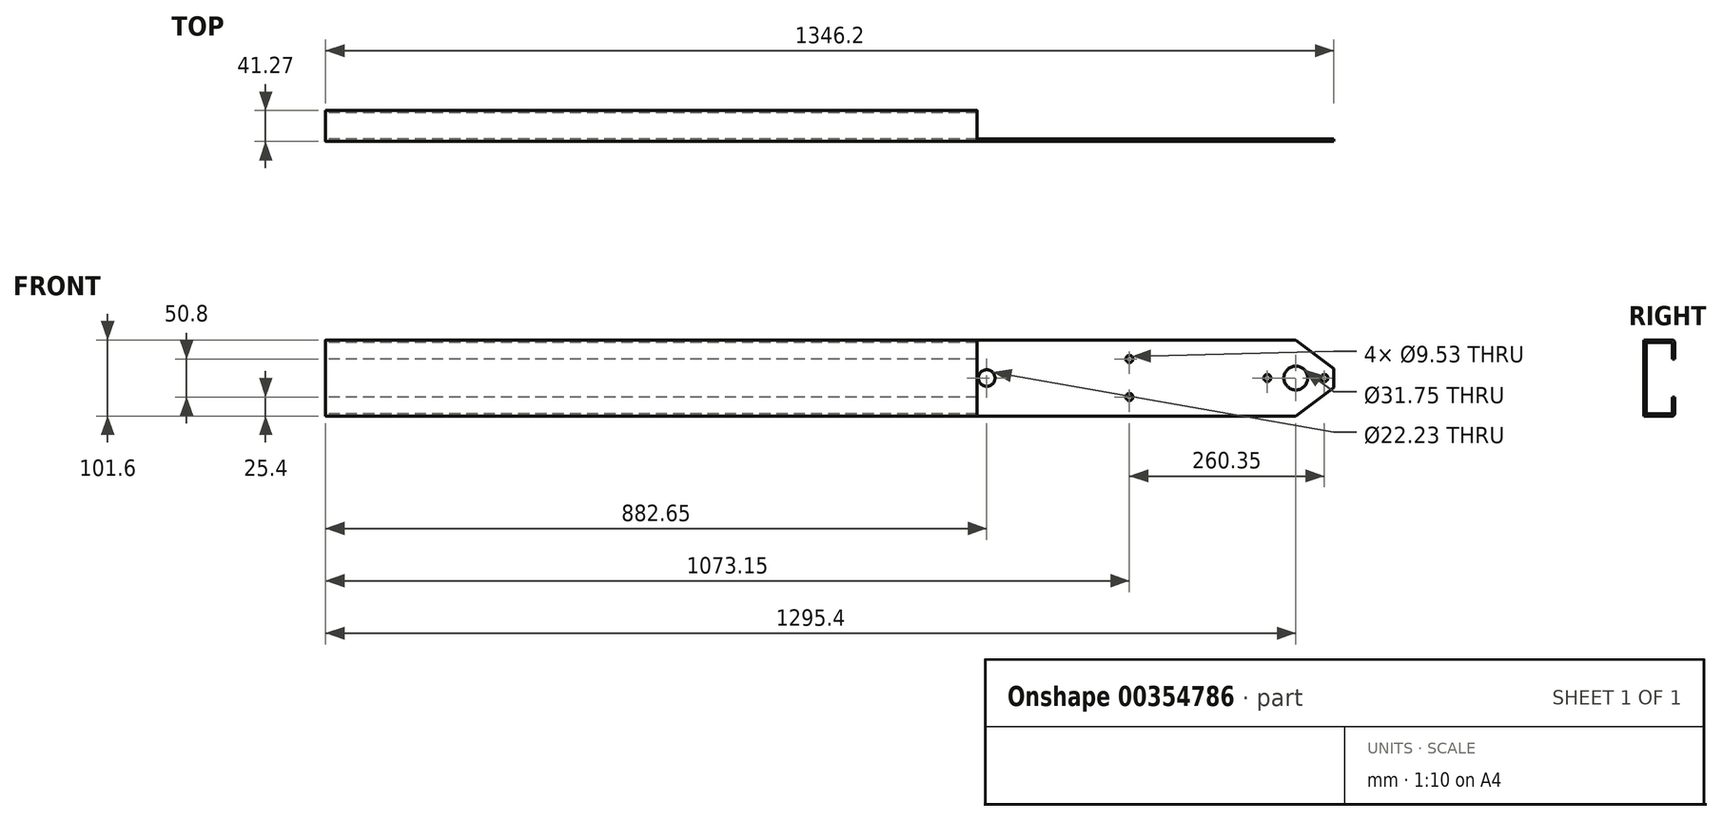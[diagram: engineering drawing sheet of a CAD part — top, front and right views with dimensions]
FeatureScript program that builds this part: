
annotation { "Feature Type Name" : "Feature", "Feature Type Description" : "" }
export const myFeature = defineFeature(function(context is Context, id is Id, definition is map)
    precondition{}
    {
        {
            var Q0;
            Q0=qCreatedBy(makeId("Right.planeOp"),FACE);
            var sketch = newSketch(context, id + "F0", { "sketchPlane" : qUnion([Q0])});
            skLineSegment(sketch, "E0", {"start": v(3.18, 0) * mm, "end": v(38.1, 0) * mm});
            skLineSegment(sketch, "E1", {"start": v(41.28, -3.17) * mm, "end": v(41.28, -25.4) * mm});
            skLineSegment(sketch, "E2", {"start": v(41.28, -25.4) * mm, "end": v(38.1, -25.4) * mm});
            skLineSegment(sketch, "E3", {"start": v(38.1, -25.4) * mm, "end": v(38.1, -3.17) * mm});
            skLineSegment(sketch, "E4", {"start": v(38.1, -3.17) * mm, "end": v(3.17, -3.18) * mm});
            skLineSegment(sketch, "E5", {"start": v(3.17, -3.17) * mm, "end": v(3.18, -98.42) * mm});
            skLineSegment(sketch, "E6", {"start": v(3.18, -98.43) * mm, "end": v(38.1, -98.43) * mm});
            skLineSegment(sketch, "E7", {"start": v(38.1, -98.43) * mm, "end": v(38.1, -76.2) * mm});
            skLineSegment(sketch, "E8", {"start": v(38.1, -76.2) * mm, "end": v(41.28, -76.2) * mm});
            skLineSegment(sketch, "E9", {"start": v(41.28, -76.2) * mm, "end": v(41.28, -98.43) * mm});
            skLineSegment(sketch, "E10", {"start": v(38.1, -101.6) * mm, "end": v(3.18, -101.6) * mm});
            skLineSegment(sketch, "E11", {"start": v(0, -98.43) * mm, "end": v(0, -3.17) * mm});
            skPoint(sketch, "E12.visualSharp", {"position": v(41.28, 0) * mm});
            skArc(sketch, "E12.filletArc", {"start": v(41.28, -3.17) * mm, "mid": v(40.35, -0.93) * mm, "end": v(38.1, 0) * mm});
            skPoint(sketch, "E13.visualSharp", {"position": v(0, 0) * mm});
            skArc(sketch, "E13.filletArc", {"start": v(3.18, 0) * mm, "mid": v(0.93, -0.93) * mm, "end": v(0, -3.17) * mm});
            skPoint(sketch, "E14.visualSharp", {"position": v(0, -101.6) * mm});
            skArc(sketch, "E14.filletArc", {"start": v(0, -98.43) * mm, "mid": v(0.93, -100.67) * mm, "end": v(3.18, -101.6) * mm});
            skPoint(sketch, "E15.visualSharp", {"position": v(41.28, -101.6) * mm});
            skArc(sketch, "E15.filletArc", {"start": v(38.1, -101.6) * mm, "mid": v(40.35, -100.67) * mm, "end": v(41.28, -98.43) * mm});
            skSolve(sketch);
        }
        {
            var Q0;
            Q0 = qSketchRegion(id + "F0", true);
            extrude(context, id + "F1", {"entities" : qUnion([Q0]), "depth" : 869.95 * mm});
        }
        {
            var Q0;
            Q0=makeQuery(id+"F1.opExtrude","SWEPT_FACE",FACE,{"disambiguationData":[OSD([sQuery(id+"F0.wireOp",EDGE,"E11")])]});
            var sketch = newSketch(context, id + "F2", { "sketchPlane" : qUnion([Q0])});
            skLineSegment(sketch, "E16.0", {"start": v(869.95, -101.6) * mm, "end": v(0, -101.6) * mm});
            skLineSegment(sketch, "E17.0", {"start": v(869.95, 0) * mm, "end": v(0, 0) * mm});
            skLineSegment(sketch, "E18", {"start": v(869.95, 0) * mm, "end": v(869.95, -101.6) * mm});
            skLineSegment(sketch, "E19", {"start": v(869.95, 0) * mm, "end": v(1346.2, 0) * mm});
            skLineSegment(sketch, "E20", {"start": v(1346.2, 0) * mm, "end": v(1346.2, -101.6) * mm});
            skLineSegment(sketch, "E21", {"start": v(1346.2, -101.6) * mm, "end": v(869.95, -101.6) * mm});
            skCircle(sketch, "E22", {"center": v(1295.4, -50.8) * mm, "radius": 15.88 * mm});
            skLineSegment(sketch, "E23", {"start": v(1346.2, -50.8) * mm, "end": v(1172.68, -50.8) * mm, "construction": true});
            skCircle(sketch, "E24", {"center": v(1257.3, -50.8) * mm, "radius": 4.76 * mm});
            skCircle(sketch, "E25", {"center": v(1333.5, -50.8) * mm, "radius": 4.76 * mm});
            skLineSegment(sketch, "E26", {"start": v(1073.15, 33.04) * mm, "end": v(1073.15, -139.91) * mm, "construction": true});
            skCircle(sketch, "E27", {"center": v(1073.15, -25.4) * mm, "radius": 4.76 * mm});
            skCircle(sketch, "E28", {"center": v(1073.15, -76.2) * mm, "radius": 4.76 * mm});
            skCircle(sketch, "E29", {"center": v(882.65, -50.8) * mm, "radius": 11.11 * mm});
            skSolve(sketch);
        }
        {
            var Q0;
            {var subQ4=sQuery(id+"F2.wireOp",EDGE,"E19");Q0=makeQuery(id+"F2.imprint","IMPRINT",FACE,{"disambiguationData":[TD([[makeQuery(id+"F2.imprint","IMPRINT",EDGE,{"derivedFrom":subQ4}),-1.0]])]});}
            extrude(context, id + "F3", {"entities" : qUnion([Q0]), "oppositeDirection" : true, "depth" : 3.17 * mm});
        }
        {
            var Q0;
            Q0=makeQuery(id+"F3.opExtrude","CAP_FACE",FACE,{"disambiguationData":[OSD([sQuery(id+"F2.wireOp",EDGE,"E18"),sQuery(id+"F2.wireOp",EDGE,"E19"),sQuery(id+"F2.wireOp",EDGE,"E20"),sQuery(id+"F2.wireOp",EDGE,"E21"),sQuery(id+"F2.wireOp",EDGE,"E22"),sQuery(id+"F2.wireOp",EDGE,"E24"),sQuery(id+"F2.wireOp",EDGE,"E25"),sQuery(id+"F2.wireOp",EDGE,"E27"),sQuery(id+"F2.wireOp",EDGE,"E28"),sQuery(id+"F2.wireOp",EDGE,"E29")])],"isStart":true});
            var sketch = newSketch(context, id + "F4", { "sketchPlane" : qUnion([Q0])});
            skLineSegment(sketch, "E30", {"start": v(1346.2, -38.1) * mm, "end": v(1295.4, 0) * mm});
            skLineSegment(sketch, "E31", {"start": v(1295.4, 0) * mm, "end": v(1346.2, 0) * mm});
            skLineSegment(sketch, "E32", {"start": v(1346.2, 0) * mm, "end": v(1346.2, -38.1) * mm});
            skLineSegment(sketch, "E33", {"start": v(1346.2, -101.6) * mm, "end": v(1346.2, -63.5) * mm});
            skLineSegment(sketch, "E34", {"start": v(1346.2, -63.5) * mm, "end": v(1295.4, -101.6) * mm});
            skLineSegment(sketch, "E35", {"start": v(1295.4, -101.6) * mm, "end": v(1346.2, -101.6) * mm});
            skSolve(sketch);
        }
        {
            var Q0;
            Q0=makeQuery(id+"F4.imprint","IMPRINT",FACE,{"disambiguationData":[TD([[makeQuery(id+"F4.imprint","IMPRINT",EDGE,{"derivedFrom":sQuery(id+"F4.wireOp",EDGE,"E30")}),-1.0]])]});
            var Q1;
            Q1=makeQuery(id+"F4.imprint","IMPRINT",FACE,{"disambiguationData":[TD([[makeQuery(id+"F4.imprint","IMPRINT",EDGE,{"derivedFrom":sQuery(id+"F4.wireOp",EDGE,"E33")}),-1.0]])]});
            var Q2;
            Q2=makeQuery(id+"F3.opExtrude","SWEPT_BODY",BODY,{"disambiguationData":[OSD([sQuery(id+"F2.wireOp",EDGE,"E18"),sQuery(id+"F2.wireOp",EDGE,"E19"),sQuery(id+"F2.wireOp",EDGE,"E20"),sQuery(id+"F2.wireOp",EDGE,"E21"),sQuery(id+"F2.wireOp",EDGE,"E22"),sQuery(id+"F2.wireOp",EDGE,"E24"),sQuery(id+"F2.wireOp",EDGE,"E25"),sQuery(id+"F2.wireOp",EDGE,"E27"),sQuery(id+"F2.wireOp",EDGE,"E28"),sQuery(id+"F2.wireOp",EDGE,"E29")])]});
            extrude(context, id + "F5", {"entities" : qUnion([Q0, Q1]), "operationType" : NewBodyOperationType.REMOVE, "endBound" : BoundingType.UP_TO_BODY, "oppositeDirection" : true, "endBoundEntityBody" : qUnion([Q2]), "depth" : 25.4 * mm});
        }
    });
